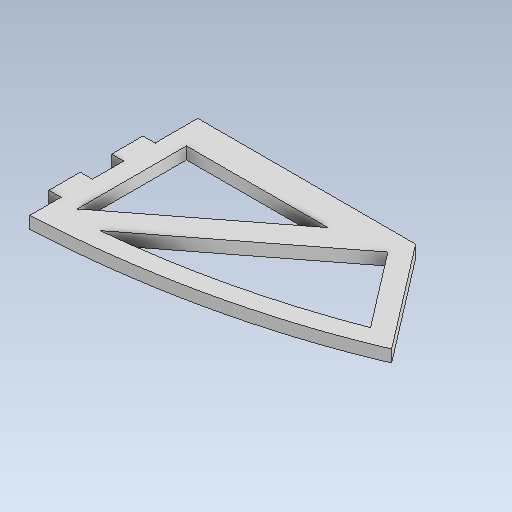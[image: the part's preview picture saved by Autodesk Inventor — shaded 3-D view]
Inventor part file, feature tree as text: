
AUTODESK INVENTOR PART (.ipt)
format: ipt  version: 2020.3 (Build 243373010, 373A)  size: 137,216 bytes
history: native  units: in
note: dims shown in document units (in); Inventor stores cm internally (conversion verified against a paired STEP export)
features: other x3, sketch x1, extrude x1
ambient origin geometry x8: Origin, YZ Plane, XZ Plane, XY Plane, X Axis, Y Axis, Z Axis, Center Point
bodies: Solid1 (feature_tree)
feature tree (5):
  other  "bulkhead_F2"
  other  "base_sketch.ipt"
  sketch  "Sketch2"  dims[d0=0.3937in d1=0.1575in d2=0.1181in d4=0.1181in d5=0.1181in d6=0.0787in d7=0.1181in d8=0.0787in d9=0.0in]
  extrude  "Extrusion1"  Depth=0.1575in
  other  "bulkhead_F2_plane"
